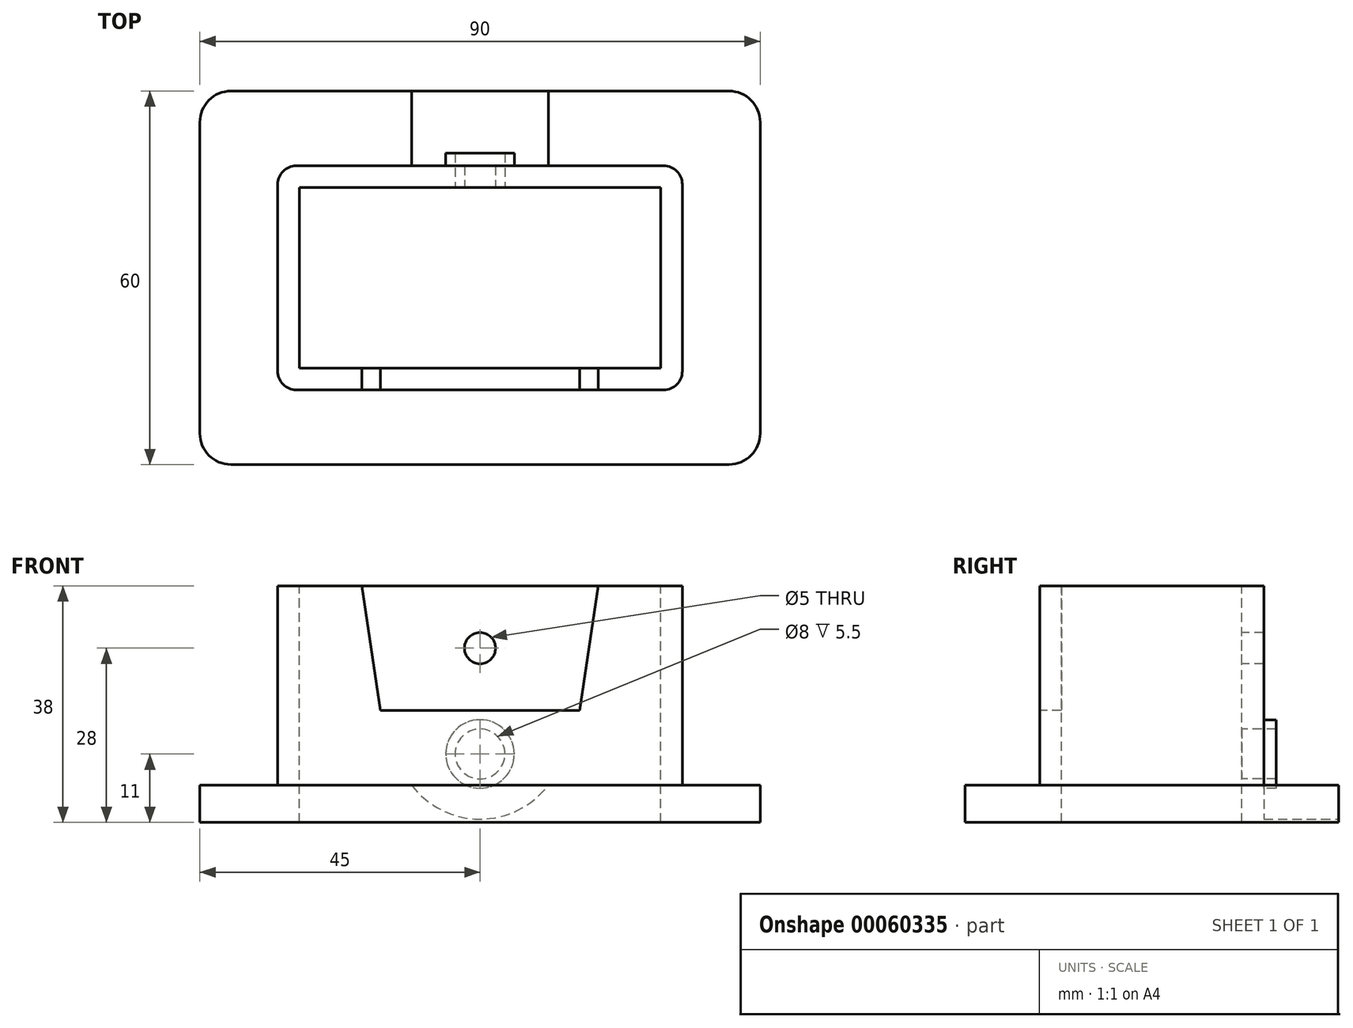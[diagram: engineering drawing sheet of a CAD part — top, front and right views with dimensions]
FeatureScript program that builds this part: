
annotation { "Feature Type Name" : "Feature", "Feature Type Description" : "" }
export const myFeature = defineFeature(function(context is Context, id is Id, definition is map)
    precondition{}
    {
        {
            var Q0;
            Q0=qCreatedBy(makeId("Top.planeOp"),FACE);
            var sketch = newSketch(context, id + "F0", { "sketchPlane" : qUnion([Q0])});
            skLineSegment(sketch, "E0.rect.bottom", {"start": v(45, -30) * mm, "end": v(-45, -30) * mm});
            skLineSegment(sketch, "E0.rect.top", {"start": v(45, 30) * mm, "end": v(-45, 30) * mm});
            skLineSegment(sketch, "E0.rect.left", {"start": v(45, -30) * mm, "end": v(45, 30) * mm});
            skLineSegment(sketch, "E0.rect.right", {"start": v(-45, -30) * mm, "end": v(-45, 30) * mm});
            skPoint(sketch, "E0.rect.middle", {"position": v(0, 0) * mm});
            skSolve(sketch);
        }
        {
            var Q0;
            Q0=makeQuery(id+"F0.imprint","IMPRINT",FACE,{"disambiguationData":[TD([[makeQuery(id+"F0.imprint","IMPRINT",EDGE,{"derivedFrom":sQuery(id+"F0.wireOp",EDGE,"E0.rect.bottom")}),-1.0]])]});
            extrude(context, id + "F1", {"entities" : qUnion([Q0]), "depth" : 6 * mm});
        }
        {
            var Q0;
            Q0=makeQuery(id+"F1.opExtrude","CAP_FACE",FACE,{"disambiguationData":[OSD([sQuery(id+"F0.wireOp",EDGE,"E0.rect.bottom"),sQuery(id+"F0.wireOp",EDGE,"E0.rect.top"),sQuery(id+"F0.wireOp",EDGE,"E0.rect.left"),sQuery(id+"F0.wireOp",EDGE,"E0.rect.right")])],"isStart":false});
            var sketch = newSketch(context, id + "F2", { "sketchPlane" : qUnion([Q0])});
            skLineSegment(sketch, "E1.rect.bottom", {"start": v(32.5, -18) * mm, "end": v(-32.5, -18) * mm});
            skLineSegment(sketch, "E1.rect.top", {"start": v(32.5, 18) * mm, "end": v(-32.5, 18) * mm});
            skLineSegment(sketch, "E1.rect.left", {"start": v(32.5, -18) * mm, "end": v(32.5, 18) * mm});
            skLineSegment(sketch, "E1.rect.right", {"start": v(-32.5, -18) * mm, "end": v(-32.5, 18) * mm});
            skPoint(sketch, "E1.rect.middle", {"position": v(0, 0) * mm});
            skSolve(sketch);
        }
        {
            var Q0;
            Q0=makeQuery(id+"F2.imprint","IMPRINT",FACE,{"disambiguationData":[TD([[makeQuery(id+"F2.imprint","IMPRINT",EDGE,{"derivedFrom":sQuery(id+"F2.wireOp",EDGE,"E1.rect.bottom")}),-1.0]])]});
            extrude(context, id + "F3", {"entities" : qUnion([Q0]), "operationType" : NewBodyOperationType.ADD, "depth" : 32 * mm});
        }
        {
            var Q0;
            Q0=makeQuery(id+"F3.opExtrude","CAP_FACE",FACE,{"disambiguationData":[OSD([sQuery(id+"F2.wireOp",EDGE,"E1.rect.bottom"),sQuery(id+"F2.wireOp",EDGE,"E1.rect.top"),sQuery(id+"F2.wireOp",EDGE,"E1.rect.left"),sQuery(id+"F2.wireOp",EDGE,"E1.rect.right")])],"isStart":false});
            var sketch = newSketch(context, id + "F4", { "sketchPlane" : qUnion([Q0])});
            skLineSegment(sketch, "E2.rect.bottom", {"start": v(29, -14.5) * mm, "end": v(-29, -14.5) * mm});
            skLineSegment(sketch, "E2.rect.top", {"start": v(29, 14.5) * mm, "end": v(-29, 14.5) * mm});
            skLineSegment(sketch, "E2.rect.left", {"start": v(29, -14.5) * mm, "end": v(29, 14.5) * mm});
            skLineSegment(sketch, "E2.rect.right", {"start": v(-29, -14.5) * mm, "end": v(-29, 14.5) * mm});
            skPoint(sketch, "E2.rect.middle", {"position": v(0, 0) * mm});
            skSolve(sketch);
        }
        {
            var Q0;
            Q0=makeQuery(id+"F4.imprint","IMPRINT",FACE,{"disambiguationData":[TD([[makeQuery(id+"F4.imprint","IMPRINT",EDGE,{"derivedFrom":sQuery(id+"F4.wireOp",EDGE,"E2.rect.bottom")}),-1.0]])]});
            extrude(context, id + "F5", {"entities" : qUnion([Q0]), "operationType" : NewBodyOperationType.REMOVE, "endBound" : BoundingType.UP_TO_NEXT, "oppositeDirection" : true, "depth" : 25 * mm});
        }
        {
            var Q0;
            Q0=makeQuery(id+"F3.opExtrude","SWEPT_FACE",FACE,{"disambiguationData":[OSD([sQuery(id+"F2.wireOp",EDGE,"E1.rect.bottom")])]});
            var sketch = newSketch(context, id + "F6", { "sketchPlane" : qUnion([Q0])});
            skLineSegment(sketch, "E3", {"start": v(-19, 38) * mm, "end": v(-16, 18) * mm});
            skLineSegment(sketch, "E4", {"start": v(-16, 18) * mm, "end": v(0, 18) * mm});
            skLineSegment(sketch, "E5", {"start": v(0, 46.04) * mm, "end": v(0, -10.02) * mm, "construction": true});
            skLineSegment(sketch, "E6.MirrorCS", {"start": v(19, 38) * mm, "end": v(16, 18) * mm});
            skLineSegment(sketch, "E7.MirrorCS", {"start": v(16, 18) * mm, "end": v(0, 18) * mm});
            skSolve(sketch);
        }
        {
            var Q0;
            {var subQ1=sQuery(id+"F6.wireOp",EDGE,"E3");Q0=makeQuery(id+"F6.imprint","IMPRINT",FACE,{"disambiguationData":[TD([[makeQuery(id+"F6.imprint","IMPRINT",EDGE,{"derivedFrom":subQ1}),1.0]])]});}
            extrude(context, id + "F7", {"entities" : qUnion([Q0]), "operationType" : NewBodyOperationType.REMOVE, "endBound" : BoundingType.UP_TO_NEXT, "oppositeDirection" : true, "depth" : 25 * mm});
        }
        {
            var Q0;
            Q0=makeQuery(id+"F5.boolean.opBoolean","COPY",FACE,{"derivedFrom":makeQuery(id+"F5.opExtrude","SWEPT_FACE",FACE,{"disambiguationData":[OSD([sQuery(id+"F4.wireOp",EDGE,"E2.rect.top")])]})});
            var sketch = newSketch(context, id + "F8", { "sketchPlane" : qUnion([Q0])});
            skCircle(sketch, "E8", {"center": v(0, 28) * mm, "radius": 2.5 * mm});
            skSolve(sketch);
        }
        {
            var Q0;
            Q0=makeQuery(id+"F8.imprint","IMPRINT",FACE,{"disambiguationData":[TD([[makeQuery(id+"F8.imprint","IMPRINT",EDGE,{"derivedFrom":sQuery(id+"F8.wireOp",EDGE,"E8")}),1.0]])]});
            extrude(context, id + "F9", {"entities" : qUnion([Q0]), "operationType" : NewBodyOperationType.REMOVE, "endBound" : BoundingType.UP_TO_NEXT, "oppositeDirection" : true, "depth" : 25 * mm});
        }
        {
            var Q0;
            Q0=makeQuery(id+"F1.opExtrude","SWEPT_FACE",FACE,{"disambiguationData":[OSD([sQuery(id+"F0.wireOp",EDGE,"E0.rect.top")])]});
            var sketch = newSketch(context, id + "F10", { "sketchPlane" : qUnion([Q0])});
            skCircle(sketch, "E9", {"center": v(0, 14.28) * mm, "radius": 13.75 * mm});
            skPoint(sketch, "E9.centerSnap0", {"position": v(0, 6) * mm});
            skLineSegment(sketch, "E10", {"start": v(0, 6) * mm, "end": v(-11, 6) * mm, "construction": true});
            skSolve(sketch);
        }
        {
            var Q0;
            {var subQ0=sQuery(id+"F10.wireOp",EDGE,"E9");var subQ1=makeQuery(id+"F1.opExtrude","CAP_EDGE",EDGE,{"disambiguationData":[OSD([sQuery(id+"F0.wireOp",EDGE,"E0.rect.top")])],"isStart":false});var subQ2=makeQuery(id+"F10.imprint","INTERSECT",VERTEX,{"disambiguationData":[OD(0.0)],"derivedFrom":[subQ1,subQ0]});Q0=makeQuery(id+"F10.imprint","IMPRINT",FACE,{"disambiguationData":[TD([[makeQuery(id+"F10.imprint","IMPRINT",EDGE,{"disambiguationData":[TD([[subQ2,-1.0]])],"derivedFrom":subQ0}),1.0]])]});}
            var Q1;
            Q1=makeQuery(id+"F3.opExtrude","SWEPT_FACE",FACE,{"disambiguationData":[OSD([sQuery(id+"F2.wireOp",EDGE,"E1.rect.top")])]});
            extrude(context, id + "F11", {"entities" : qUnion([Q0]), "operationType" : NewBodyOperationType.REMOVE, "endBound" : BoundingType.UP_TO_SURFACE, "oppositeDirection" : true, "endBoundEntityFace" : qUnion([Q1]), "depth" : 25 * mm});
        }
        {
            var Q0;
            Q0=makeQuery(id+"F11.boolean.opBoolean","MERGE",FACE,{"derivedFrom":[makeQuery(id+"F3.opExtrude","SWEPT_FACE",FACE,{"disambiguationData":[OSD([sQuery(id+"F2.wireOp",EDGE,"E1.rect.top")])]}),makeQuery(id+"F11.opExtrude","CAP_FACE",FACE,{"disambiguationData":[OSD([sQuery(id+"F0.wireOp",EDGE,"E0.rect.top"),sQuery(id+"F10.wireOp",EDGE,"E9")])],"isStart":false})]});
            var sketch = newSketch(context, id + "F12", { "sketchPlane" : qUnion([Q0])});
            skCircle(sketch, "E11", {"center": v(0, 11) * mm, "radius": 5.5 * mm});
            skCircle(sketch, "E12", {"center": v(0, 11) * mm, "radius": 4 * mm});
            skSolve(sketch);
        }
        {
            var Q0;
            Q0=makeQuery(id+"F12.imprint","IMPRINT",FACE,{"disambiguationData":[TD([[makeQuery(id+"F12.imprint","IMPRINT",EDGE,{"derivedFrom":sQuery(id+"F12.wireOp",EDGE,"E11")}),1.0]])]});
            extrude(context, id + "F13", {"entities" : qUnion([Q0]), "operationType" : NewBodyOperationType.ADD, "depth" : 2 * mm});
        }
        {
            var Q0;
            Q0=makeQuery(id+"F13.boolean.opBoolean","SPLIT",FACE,{"disambiguationData":[TD([makeQuery(id+"F13.opExtrude","SWEPT_FACE",FACE,{"disambiguationData":[OSD([sQuery(id+"F12.wireOp",EDGE,"E12")])]})])],"derivedFrom":makeQuery(id+"F11.boolean.opBoolean","MERGE",FACE,{"derivedFrom":[makeQuery(id+"F3.opExtrude","SWEPT_FACE",FACE,{"disambiguationData":[OSD([sQuery(id+"F2.wireOp",EDGE,"E1.rect.top")])]}),makeQuery(id+"F11.opExtrude","CAP_FACE",FACE,{"disambiguationData":[OSD([sQuery(id+"F0.wireOp",EDGE,"E0.rect.top"),sQuery(id+"F10.wireOp",EDGE,"E9")])],"isStart":false})]})});
            extrude(context, id + "F14", {"entities" : qUnion([Q0]), "operationType" : NewBodyOperationType.REMOVE, "oppositeDirection" : true, "depth" : 25 * mm});
        }
        {
            var Q0;
            Q0=makeQuery(id+"F1.opExtrude","SWEPT_EDGE",EDGE,{"disambiguationData":[OSD([sQuery(id+"F0.wireOp",EDGE,"E0.rect.bottom"),sQuery(id+"F0.wireOp",EDGE,"E0.rect.left")])]});
            var Q1;
            Q1=makeQuery(id+"F1.opExtrude","SWEPT_EDGE",EDGE,{"disambiguationData":[OSD([sQuery(id+"F0.wireOp",EDGE,"E0.rect.top"),sQuery(id+"F0.wireOp",EDGE,"E0.rect.left")])]});
            var Q2;
            Q2=makeQuery(id+"F1.opExtrude","SWEPT_EDGE",EDGE,{"disambiguationData":[OSD([sQuery(id+"F0.wireOp",EDGE,"E0.rect.bottom"),sQuery(id+"F0.wireOp",EDGE,"E0.rect.right")])]});
            var Q3;
            Q3=makeQuery(id+"F1.opExtrude","SWEPT_EDGE",EDGE,{"disambiguationData":[OSD([sQuery(id+"F0.wireOp",EDGE,"E0.rect.top"),sQuery(id+"F0.wireOp",EDGE,"E0.rect.right")])]});
            fillet(context, id + "F15", {"entities" : qUnion([Q0, Q1, Q2, Q3]), "radius" : 5 * mm, "tangentPropagation" : true, "allowEdgeOverflow" : false});
        }
        {
            var Q0;
            Q0=makeQuery(id+"F3.opExtrude","SWEPT_EDGE",EDGE,{"disambiguationData":[OSD([sQuery(id+"F2.wireOp",EDGE,"E1.rect.top"),sQuery(id+"F2.wireOp",EDGE,"E1.rect.right")])]});
            var Q1;
            Q1=makeQuery(id+"F3.opExtrude","SWEPT_EDGE",EDGE,{"disambiguationData":[OSD([sQuery(id+"F2.wireOp",EDGE,"E1.rect.bottom"),sQuery(id+"F2.wireOp",EDGE,"E1.rect.right")])]});
            var Q2;
            Q2=makeQuery(id+"F3.opExtrude","SWEPT_EDGE",EDGE,{"disambiguationData":[OSD([sQuery(id+"F2.wireOp",EDGE,"E1.rect.top"),sQuery(id+"F2.wireOp",EDGE,"E1.rect.left")])]});
            var Q3;
            Q3=makeQuery(id+"F3.opExtrude","SWEPT_EDGE",EDGE,{"disambiguationData":[OSD([sQuery(id+"F2.wireOp",EDGE,"E1.rect.bottom"),sQuery(id+"F2.wireOp",EDGE,"E1.rect.left")])]});
            var Q4;
            Q4=makeQuery(id+"F7.boolean.opBoolean","COPY",EDGE,{"derivedFrom":makeQuery(id+"F7.opExtrude","CAP_EDGE",EDGE,{"disambiguationData":[OSD([sQuery(id+"F6.wireOp",EDGE,"E3")])],"isStart":true})});
            var Q5;
            Q5=makeQuery(id+"F7.boolean.opBoolean","COPY",EDGE,{"derivedFrom":makeQuery(id+"F7.opExtrude","CAP_EDGE",EDGE,{"disambiguationData":[OSD([sQuery(id+"F6.wireOp",EDGE,"E6.MirrorCS")])],"isStart":true})});
            var Q6;
            Q6=makeQuery(id+"F7.boolean.opBoolean","COPY",EDGE,{"derivedFrom":makeQuery(id+"F7.opExtrude","CAP_EDGE",EDGE,{"disambiguationData":[OSD([sQuery(id+"F6.wireOp",EDGE,"E4"),sQuery(id+"F6.wireOp",EDGE,"E7.MirrorCS")])],"isStart":true})});
            fillet(context, id + "F16", {"entities" : qUnion([Q0, Q1, Q2, Q3, Q4, Q5, Q6]), "radius" : 3 * mm, "tangentPropagation" : true, "allowEdgeOverflow" : false});
        }
    });
